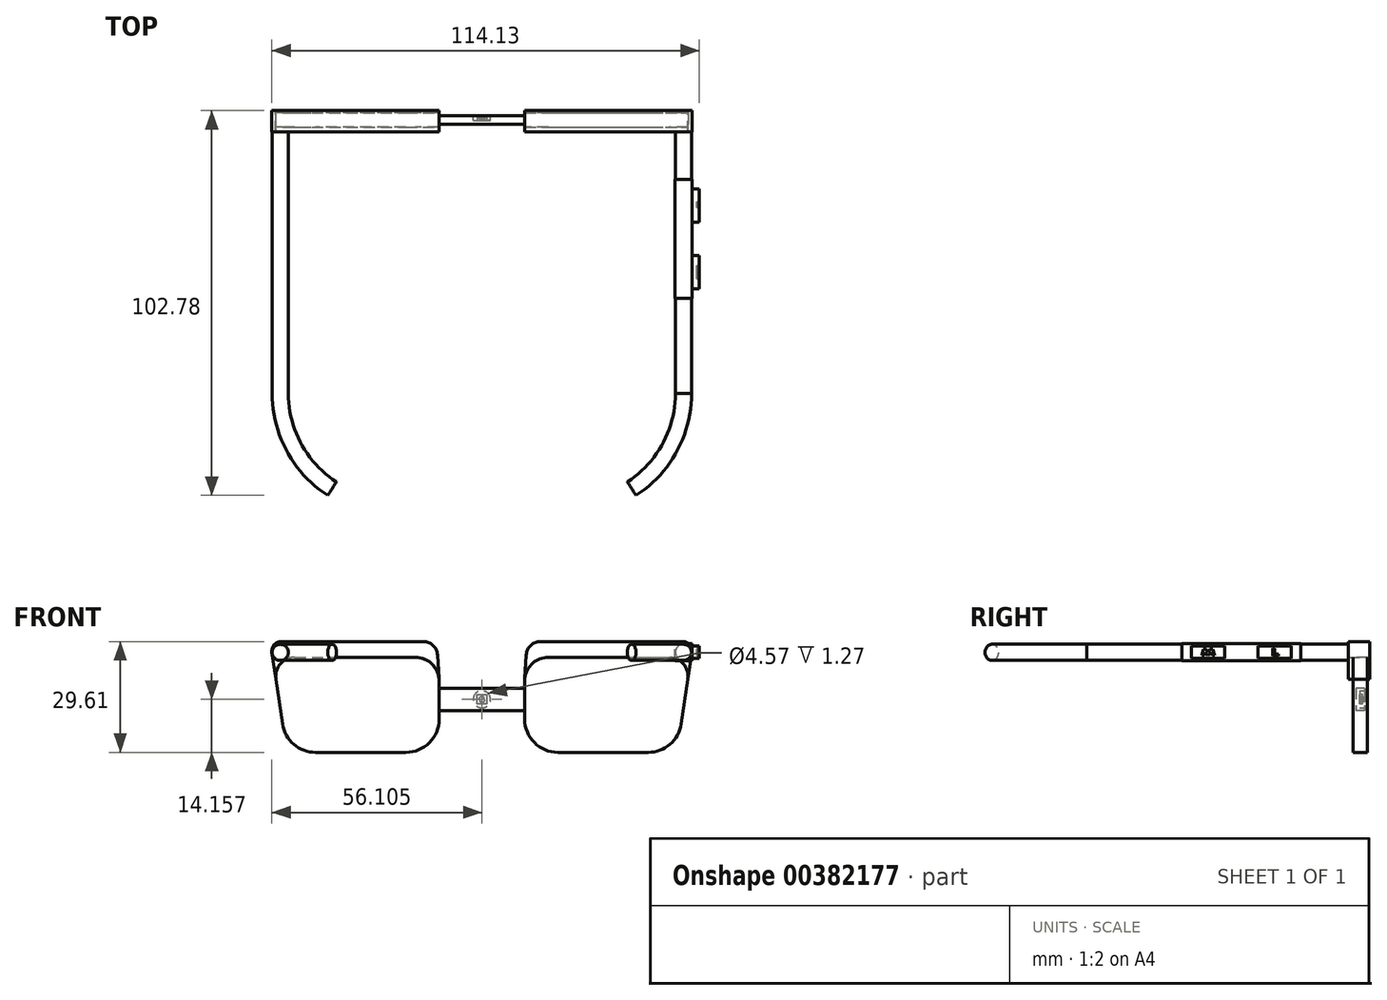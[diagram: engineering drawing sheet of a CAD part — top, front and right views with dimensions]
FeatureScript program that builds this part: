
annotation { "Feature Type Name" : "Feature", "Feature Type Description" : "" }
export const myFeature = defineFeature(function(context is Context, id is Id, definition is map)
    precondition{}
    {
        {
            var Q0;
            Q0=qCreatedBy(makeId("Front.planeOp"),FACE);
            var sketch = newSketch(context, id + "F0", { "sketchPlane" : qUnion([Q0])});
            skLineSegment(sketch, "E0", {"start": v(-55.04, 50.03) * mm, "end": v(-22.83, 50.03) * mm});
            skLineSegment(sketch, "E1", {"start": v(-16.48, 43.68) * mm, "end": v(-16.48, 33.52) * mm});
            skLineSegment(sketch, "E2", {"start": v(-25.37, 24.63) * mm, "end": v(-49.47, 24.63) * mm});
            skLineSegment(sketch, "E3", {"start": v(-58.26, 32.2) * mm, "end": v(-60.06, 44.2) * mm});
            skLineSegment(sketch, "E4", {"start": v(6.38, 43.68) * mm, "end": v(6.38, 33.52) * mm});
            skLineSegment(sketch, "E5", {"start": v(12.73, 50.03) * mm, "end": v(44.93, 50.03) * mm});
            skLineSegment(sketch, "E6", {"start": v(15.27, 24.63) * mm, "end": v(39.36, 24.63) * mm});
            skLineSegment(sketch, "E7", {"start": v(48.15, 32.2) * mm, "end": v(49.95, 44.2) * mm});
            skPoint(sketch, "E8.visualSharp", {"position": v(-16.48, 50.03) * mm});
            skArc(sketch, "E8.filletArc", {"start": v(-16.48, 43.68) * mm, "mid": v(-18.34, 48.17) * mm, "end": v(-22.83, 50.03) * mm});
            skPoint(sketch, "E9.visualSharp", {"position": v(6.38, 50.03) * mm});
            skArc(sketch, "E9.filletArc", {"start": v(12.73, 50.03) * mm, "mid": v(8.23, 48.17) * mm, "end": v(6.38, 43.68) * mm});
            skPoint(sketch, "E10.visualSharp", {"position": v(-16.48, 24.63) * mm});
            skArc(sketch, "E10.filletArc", {"start": v(-25.37, 24.63) * mm, "mid": v(-19.09, 27.23) * mm, "end": v(-16.48, 33.52) * mm});
            skPoint(sketch, "E11.visualSharp", {"position": v(-57.12, 24.63) * mm});
            skArc(sketch, "E11.filletArc", {"start": v(-58.26, 32.2) * mm, "mid": v(-55.27, 26.78) * mm, "end": v(-49.47, 24.63) * mm});
            skPoint(sketch, "E12.visualSharp", {"position": v(6.38, 24.63) * mm});
            skArc(sketch, "E12.filletArc", {"start": v(6.38, 33.52) * mm, "mid": v(8.98, 27.23) * mm, "end": v(15.27, 24.63) * mm});
            skPoint(sketch, "E13.visualSharp", {"position": v(47.02, 24.63) * mm});
            skArc(sketch, "E13.filletArc", {"start": v(39.36, 24.63) * mm, "mid": v(45.16, 26.78) * mm, "end": v(48.15, 32.2) * mm});
            skPoint(sketch, "E14.visualSharp", {"position": v(-60.93, 50.03) * mm});
            skArc(sketch, "E14.filletArc", {"start": v(-55.04, 50.03) * mm, "mid": v(-58.89, 48.26) * mm, "end": v(-60.06, 44.2) * mm});
            skPoint(sketch, "E15.visualSharp", {"position": v(50.83, 50.03) * mm});
            skArc(sketch, "E15.filletArc", {"start": v(49.95, 44.2) * mm, "mid": v(48.78, 48.26) * mm, "end": v(44.93, 50.03) * mm});
            skLineSegment(sketch, "E16", {"start": v(-16.48, 41.77) * mm, "end": v(6.38, 41.77) * mm});
            skLineSegment(sketch, "E17", {"start": v(-16.48, 35.8) * mm, "end": v(6.38, 35.8) * mm});
            skSolve(sketch);
        }
        {
            var Q0;
            Q0=makeQuery(id+"F0.imprint","IMPRINT",FACE,{"disambiguationData":[TD([[makeQuery(id+"F0.imprint","IMPRINT",EDGE,{"derivedFrom":sQuery(id+"F0.wireOp",EDGE,"E0")}),-1.0]])]});
            var Q1;
            Q1=makeQuery(id+"F0.imprint","IMPRINT",FACE,{"disambiguationData":[TD([[makeQuery(id+"F0.imprint","IMPRINT",EDGE,{"derivedFrom":sQuery(id+"F0.wireOp",EDGE,"E5")}),-1.0]])]});
            extrude(context, id + "F1", {"entities" : qUnion([Q0, Q1]), "oppositeDirection" : true, "depth" : 3.8 * mm});
        }
        {
            var Q0;
            {var subQ0=sQuery(id+"F0.wireOp",EDGE,"E16");Q0=makeQuery(id+"F0.imprint","IMPRINT",FACE,{"disambiguationData":[TD([[makeQuery(id+"F0.imprint","IMPRINT",EDGE,{"derivedFrom":subQ0}),-1.0]])]});}
            extrude(context, id + "F2", {"entities" : qUnion([Q0]), "oppositeDirection" : true, "depth" : 3.05 * mm});
        }
        {
            var Q0;
            Q0=makeQuery(id+"F2.opExtrude","CAP_FACE",FACE,{"disambiguationData":[OSD([sQuery(id+"F0.wireOp",EDGE,"E1"),sQuery(id+"F0.wireOp",EDGE,"E4"),sQuery(id+"F0.wireOp",EDGE,"E16"),sQuery(id+"F0.wireOp",EDGE,"E17")])],"isStart":true});
            extrude(context, id + "F3", {"entities" : qUnion([Q0]), "operationType" : NewBodyOperationType.REMOVE, "oppositeDirection" : true, "depth" : 0.76 * mm});
        }
        {
            var Q0;
            Q0=qCreatedBy(makeId("Front.planeOp"),FACE);
            var sketch = newSketch(context, id + "F4", { "sketchPlane" : qUnion([Q0])});
            skLineSegment(sketch, "E18.0", {"start": v(-55.04, 50.03) * mm, "end": v(-22.83, 50.03) * mm});
            skArc(sketch, "E19.0", {"start": v(-55.04, 50.03) * mm, "mid": v(-58.89, 48.26) * mm, "end": v(-60.06, 44.2) * mm});
            skArc(sketch, "E20.0", {"start": v(-16.48, 43.68) * mm, "mid": v(-18.34, 48.17) * mm, "end": v(-22.83, 50.03) * mm});
            skArc(sketch, "E21.0", {"start": v(12.73, 50.03) * mm, "mid": v(8.23, 48.17) * mm, "end": v(6.38, 43.68) * mm});
            skLineSegment(sketch, "E22.0", {"start": v(12.73, 50.03) * mm, "end": v(44.93, 50.03) * mm});
            skArc(sketch, "E23.0", {"start": v(49.95, 44.2) * mm, "mid": v(48.78, 48.26) * mm, "end": v(44.93, 50.03) * mm});
            skLineSegment(sketch, "E24", {"start": v(-60.06, 44.2) * mm, "end": v(-61.13, 51.32) * mm});
            skLineSegment(sketch, "E25", {"start": v(49.95, 44.2) * mm, "end": v(51.02, 51.32) * mm});
            skLineSegment(sketch, "E26", {"start": v(-58.62, 54.24) * mm, "end": v(-20.7, 54.24) * mm});
            skLineSegment(sketch, "E27", {"start": v(48.5, 54.24) * mm, "end": v(10.6, 54.24) * mm});
            skLineSegment(sketch, "E28", {"start": v(-16.9, 50.66) * mm, "end": v(-16.48, 43.68) * mm});
            skLineSegment(sketch, "E29", {"start": v(6.8, 50.66) * mm, "end": v(6.38, 43.68) * mm});
            skPoint(sketch, "E30.visualSharp", {"position": v(-61.57, 54.24) * mm});
            skArc(sketch, "E30.filletArc", {"start": v(-58.62, 54.24) * mm, "mid": v(-60.54, 53.36) * mm, "end": v(-61.13, 51.32) * mm});
            skPoint(sketch, "E31.visualSharp", {"position": v(-17.12, 54.24) * mm});
            skArc(sketch, "E31.filletArc", {"start": v(-16.9, 50.66) * mm, "mid": v(-18.1, 53.2) * mm, "end": v(-20.7, 54.24) * mm});
            skPoint(sketch, "E32.visualSharp", {"position": v(7, 54.24) * mm});
            skArc(sketch, "E32.filletArc", {"start": v(10.6, 54.24) * mm, "mid": v(7.98, 53.2) * mm, "end": v(6.8, 50.66) * mm});
            skPoint(sketch, "E33.visualSharp", {"position": v(51.46, 54.24) * mm});
            skArc(sketch, "E33.filletArc", {"start": v(51.02, 51.32) * mm, "mid": v(50.43, 53.36) * mm, "end": v(48.5, 54.24) * mm});
            skSolve(sketch);
        }
        {
            var Q0;
            {var subQ1=sQuery(id+"F4.wireOp",EDGE,"E18.0");Q0=makeQuery(id+"F4.imprint","IMPRINT",FACE,{"disambiguationData":[TD([[makeQuery(id+"F4.imprint","IMPRINT",EDGE,{"derivedFrom":subQ1}),1.0]])]});}
            var Q1;
            {var subQ1=sQuery(id+"F4.wireOp",EDGE,"E22.0");Q1=makeQuery(id+"F4.imprint","IMPRINT",FACE,{"disambiguationData":[TD([[makeQuery(id+"F4.imprint","IMPRINT",EDGE,{"derivedFrom":subQ1}),1.0]])]});}
            extrude(context, id + "F5", {"entities" : qUnion([Q0, Q1]), "depth" : 1.27 * mm, "hasSecondDirection" : true, "secondDirectionOppositeDirection" : true, "secondDirectionDepth" : 4.44 * mm});
        }
        {
            var Q0;
            Q0=makeQuery(id+"F5.opExtrude","CAP_FACE",FACE,{"disambiguationData":[OSD([sQuery(id+"F4.wireOp",EDGE,"E18.0"),sQuery(id+"F4.wireOp",EDGE,"E19.0"),sQuery(id+"F4.wireOp",EDGE,"E20.0"),sQuery(id+"F4.wireOp",EDGE,"E24"),sQuery(id+"F4.wireOp",EDGE,"E26"),sQuery(id+"F4.wireOp",EDGE,"E28"),sQuery(id+"F4.wireOp",EDGE,"E30.filletArc"),sQuery(id+"F4.wireOp",EDGE,"E31.filletArc")])],"isStart":false});
            var sketch = newSketch(context, id + "F6", { "sketchPlane" : qUnion([Q0])});
            skCircle(sketch, "E34", {"center": v(-58.89, 51.32) * mm, "radius": 2.16 * mm});
            skPoint(sketch, "E34.centerSnap0", {"position": v(-58.89, 48.26) * mm});
            skLineSegment(sketch, "E35.0", {"start": v(49.95, 44.2) * mm, "end": v(51.02, 51.32) * mm});
            skArc(sketch, "E36.0", {"start": v(49.95, 44.2) * mm, "mid": v(48.78, 48.26) * mm, "end": v(44.93, 50.03) * mm});
            skCircle(sketch, "E37", {"center": v(48.78, 51.32) * mm, "radius": 2.16 * mm});
            skPoint(sketch, "E37.centerSnap0", {"position": v(48.78, 48.26) * mm});
            skSolve(sketch);
        }
        {
            var Q0;
            Q0=makeQuery(id+"F6.imprint","IMPRINT",FACE,{"disambiguationData":[TD([[makeQuery(id+"F6.imprint","IMPRINT",EDGE,{"derivedFrom":sQuery(id+"F6.wireOp",EDGE,"E34")}),1.0]])]});
            extrude(context, id + "F7", {"entities" : qUnion([Q0]), "operationType" : NewBodyOperationType.ADD, "depth" : 69.85 * mm});
        }
        {
            var Q0;
            Q0=makeQuery(id+"F6.imprint","IMPRINT",FACE,{"disambiguationData":[TD([[makeQuery(id+"F6.imprint","IMPRINT",EDGE,{"derivedFrom":sQuery(id+"F6.wireOp",EDGE,"E37")}),1.0]])]});
            extrude(context, id + "F8", {"entities" : qUnion([Q0]), "depth" : 12.7 * mm});
        }
        {
            var Q0;
            Q0=makeQuery(id+"F8.opExtrude","CAP_FACE",FACE,{"disambiguationData":[OSD([sQuery(id+"F6.wireOp",EDGE,"E37")])],"isStart":false});
            var sketch = newSketch(context, id + "F9", { "sketchPlane" : qUnion([Q0])});
            skLineSegment(sketch, "E38", {"start": v(48.78, 51.32) * mm, "end": v(46.49, 51.32) * mm});
            skLineSegment(sketch, "E39", {"start": v(48.78, 51.32) * mm, "end": v(48.78, 49.04) * mm});
            skLineSegment(sketch, "E40", {"start": v(46.49, 51.32) * mm, "end": v(46.49, 49.04) * mm});
            skLineSegment(sketch, "E41", {"start": v(46.49, 49.04) * mm, "end": v(48.78, 49.04) * mm});
            skLineSegment(sketch, "E42", {"start": v(46.49, 51.32) * mm, "end": v(46.49, 53.6) * mm});
            skLineSegment(sketch, "E43", {"start": v(46.49, 53.6) * mm, "end": v(51.06, 53.6) * mm});
            skLineSegment(sketch, "E44", {"start": v(51.06, 53.6) * mm, "end": v(51.06, 49.04) * mm});
            skLineSegment(sketch, "E45", {"start": v(51.06, 49.04) * mm, "end": v(48.78, 49.04) * mm});
            skSolve(sketch);
        }
        {
            var Q0;
            {var subQ4=sQuery(id+"F9.wireOp",EDGE,"E42");Q0=makeQuery(id+"F9.imprint","IMPRINT",FACE,{"disambiguationData":[TD([[makeQuery(id+"F9.imprint","IMPRINT",EDGE,{"derivedFrom":subQ4}),-1.0]])]});}
            var Q1;
            {var subQ0=sQuery(id+"F9.wireOp",EDGE,"E39");var subQ1=sQuery(id+"F9.wireOp",EDGE,"E38");var subQ2=makeQuery(id+"F9.imprint","INTERSECT",VERTEX,{"derivedFrom":[subQ1,subQ0]});Q1=makeQuery(id+"F9.imprint","IMPRINT",FACE,{"disambiguationData":[TD([[makeQuery(id+"F9.imprint","IMPRINT",EDGE,{"disambiguationData":[TD([[subQ2,-1.0]])],"derivedFrom":subQ1}),-1.0]])]});}
            var Q2;
            {var subQ0=sQuery(id+"F9.wireOp",EDGE,"E39");var subQ1=sQuery(id+"F9.wireOp",EDGE,"E38");var subQ2=makeQuery(id+"F9.imprint","INTERSECT",VERTEX,{"derivedFrom":[subQ1,subQ0]});Q2=makeQuery(id+"F9.imprint","IMPRINT",FACE,{"disambiguationData":[TD([[makeQuery(id+"F9.imprint","IMPRINT",EDGE,{"disambiguationData":[TD([[subQ2,-1.0]])],"derivedFrom":subQ1}),1.0]])]});}
            var Q3;
            {var subQ1=sQuery(id+"F9.wireOp",EDGE,"E40");Q3=makeQuery(id+"F9.imprint","IMPRINT",FACE,{"disambiguationData":[TD([[makeQuery(id+"F9.imprint","IMPRINT",EDGE,{"derivedFrom":subQ1}),1.0]])]});}
            extrude(context, id + "F10", {"entities" : qUnion([Q0, Q1, Q2, Q3]), "operationType" : NewBodyOperationType.ADD, "depth" : 31.75 * mm});
        }
        {
            var Q0;
            Q0=makeQuery(id+"F10.opExtrude","CAP_FACE",FACE,{"disambiguationData":[OSD([sQuery(id+"F9.wireOp",EDGE,"E40"),sQuery(id+"F9.wireOp",EDGE,"E41"),sQuery(id+"F9.wireOp",EDGE,"E42"),sQuery(id+"F9.wireOp",EDGE,"E43"),sQuery(id+"F9.wireOp",EDGE,"E44"),sQuery(id+"F9.wireOp",EDGE,"E45")])],"isStart":false});
            var sketch = newSketch(context, id + "F11", { "sketchPlane" : qUnion([Q0])});
            skCircle(sketch, "E46", {"center": v(48.78, 51.32) * mm, "radius": 2.16 * mm});
            skPoint(sketch, "E46.centerSnap0", {"position": v(51.06, 51.32) * mm});
            skPoint(sketch, "E46.centerSnap1", {"position": v(48.78, 49.04) * mm});
            skSolve(sketch);
        }
        {
            var Q0;
            Q0=makeQuery(id+"F11.imprint","IMPRINT",FACE,{"disambiguationData":[TD([[makeQuery(id+"F11.imprint","IMPRINT",EDGE,{"derivedFrom":sQuery(id+"F11.wireOp",EDGE,"E46")}),1.0]])]});
            extrude(context, id + "F12", {"entities" : qUnion([Q0]), "operationType" : NewBodyOperationType.ADD, "depth" : 25.4 * mm});
        }
        {
            var Q0;
            Q0=makeQuery(id+"F2.opExtrude","CAP_FACE",FACE,{"disambiguationData":[OSD([sQuery(id+"F0.wireOp",EDGE,"E1"),sQuery(id+"F0.wireOp",EDGE,"E4"),sQuery(id+"F0.wireOp",EDGE,"E16"),sQuery(id+"F0.wireOp",EDGE,"E17")])],"isStart":false});
            var sketch = newSketch(context, id + "F13", { "sketchPlane" : qUnion([Q0])});
            skCircle(sketch, "E47", {"center": v(5.05, 38.79) * mm, "radius": 2.29 * mm});
            skPoint(sketch, "E47.centerSnap0", {"position": v(5.05, 35.8) * mm});
            skPoint(sketch, "E47.centerSnap1", {"position": v(-6.38, 38.79) * mm});
            skSolve(sketch);
        }
        {
            var Q0;
            Q0=makeQuery(id+"F13.imprint","IMPRINT",FACE,{"disambiguationData":[TD([[makeQuery(id+"F13.imprint","IMPRINT",EDGE,{"derivedFrom":sQuery(id+"F13.wireOp",EDGE,"E47")}),1.0]])]});
            extrude(context, id + "F14", {"entities" : qUnion([Q0]), "operationType" : NewBodyOperationType.REMOVE, "oppositeDirection" : true, "depth" : 1.27 * mm});
        }
        {
            var Q0;
            Q0=makeQuery(id+"F14.boolean.opBoolean","COPY",FACE,{"derivedFrom":makeQuery(id+"F14.opExtrude","CAP_FACE",FACE,{"disambiguationData":[OSD([sQuery(id+"F13.wireOp",EDGE,"E47")])],"isStart":false})});
            var sketch = newSketch(context, id + "F15", { "sketchPlane" : qUnion([Q0])});
            skLineSegment(sketch, "E48", {"start": v(5.05, 38.79) * mm, "end": v(6.32, 38.79) * mm});
            skLineSegment(sketch, "E49", {"start": v(6.32, 38.79) * mm, "end": v(6.32, 40.06) * mm});
            skLineSegment(sketch, "E50", {"start": v(6.32, 40.06) * mm, "end": v(3.8, 40.06) * mm});
            skLineSegment(sketch, "E51", {"start": v(3.8, 40.06) * mm, "end": v(3.8, 37.52) * mm});
            skLineSegment(sketch, "E52", {"start": v(3.8, 37.52) * mm, "end": v(6.32, 37.52) * mm});
            skLineSegment(sketch, "E53", {"start": v(6.32, 37.52) * mm, "end": v(6.32, 38.79) * mm});
            skSolve(sketch);
        }
        {
            var Q0;
            Q0=makeQuery(id+"F15.imprint","IMPRINT",FACE,{"disambiguationData":[TD([[makeQuery(id+"F15.imprint","IMPRINT",EDGE,{"derivedFrom":sQuery(id+"F15.wireOp",EDGE,"E49")}),1.0]])]});
            extrude(context, id + "F16", {"entities" : qUnion([Q0]), "operationType" : NewBodyOperationType.ADD, "depth" : 0.76 * mm});
        }
        {
            var Q0;
            Q0=makeQuery(id+"F16.opExtrude","CAP_FACE",FACE,{"disambiguationData":[OSD([sQuery(id+"F15.wireOp",EDGE,"E49"),sQuery(id+"F15.wireOp",EDGE,"E50"),sQuery(id+"F15.wireOp",EDGE,"E51"),sQuery(id+"F15.wireOp",EDGE,"E52"),sQuery(id+"F15.wireOp",EDGE,"E53")])],"isStart":false});
            var sketch = newSketch(context, id + "F17", { "sketchPlane" : qUnion([Q0])});
            skCircle(sketch, "E54.cCircle", {"center": v(5.06, 38.79) * mm, "radius": 0.7 * mm, "construction": true});
            skPoint(sketch, "E54.cCircle.centerSnap0", {"position": v(5.06, 37.52) * mm});
            skPoint(sketch, "E54.cCircle.centerSnap1", {"position": v(3.8, 38.79) * mm});
            skLineSegment(sketch, "E54.0", {"start": v(5.75, 38.37) * mm, "end": v(5.04, 37.98) * mm});
            skLineSegment(sketch, "E54.1", {"start": v(5.04, 37.98) * mm, "end": v(4.35, 38.4) * mm});
            skLineSegment(sketch, "E54.2", {"start": v(4.35, 38.4) * mm, "end": v(4.37, 39.2) * mm});
            skLineSegment(sketch, "E54.3", {"start": v(4.37, 39.2) * mm, "end": v(5.08, 39.6) * mm});
            skLineSegment(sketch, "E54.4", {"start": v(5.08, 39.6) * mm, "end": v(5.77, 39.17) * mm});
            skLineSegment(sketch, "E54.5", {"start": v(5.77, 39.17) * mm, "end": v(5.75, 38.37) * mm});
            skPoint(sketch, "E54.0.midPoint", {"position": v(5.4, 38.18) * mm});
            skSolve(sketch);
        }
        {
            var Q0;
            Q0=makeQuery(id+"F17.imprint","IMPRINT",FACE,{"disambiguationData":[TD([[makeQuery(id+"F17.imprint","IMPRINT",EDGE,{"derivedFrom":sQuery(id+"F17.wireOp",EDGE,"E54.0")}),-1.0]])]});
            extrude(context, id + "F18", {"entities" : qUnion([Q0]), "operationType" : NewBodyOperationType.REMOVE, "oppositeDirection" : true, "depth" : 0.38 * mm});
        }
        {
            var Q0;
            Q0=makeQuery(id+"F12.opExtrude","CAP_FACE",FACE,{"disambiguationData":[OSD([sQuery(id+"F11.wireOp",EDGE,"E46")])],"isStart":false});
            extrude(context, id + "F19", {"entities" : qUnion([Q0]), "depth" : 5.08 * mm});
        }
        {
            var Q0;
            Q0=makeQuery(id+"F19.opExtrude","SWEPT_BODY",BODY,{"disambiguationData":[OSD([sQuery(id+"F11.wireOp",EDGE,"E46")])]});
            deleteBodies(context, id + "F20", {"entities" : qUnion([Q0])});
        }
        {
            var Q0;
            Q0=makeQuery(id+"F10.opExtrude","SWEPT_FACE",FACE,{"disambiguationData":[OSD([sQuery(id+"F9.wireOp",EDGE,"E44")])]});
            var sketch = newSketch(context, id + "F21", { "sketchPlane" : qUnion([Q0])});
            skLineSegment(sketch, "E55.0", {"start": v(-45.72, 53.6) * mm, "end": v(-13.97, 53.6) * mm});
            skLineSegment(sketch, "E56.0", {"start": v(-45.72, 49.04) * mm, "end": v(-13.97, 49.04) * mm});
            skLineSegment(sketch, "E57.0", {"start": v(-13.97, 53.6) * mm, "end": v(-13.97, 49.04) * mm});
            skLineSegment(sketch, "E58.0", {"start": v(-45.72, 53.6) * mm, "end": v(-45.72, 49.04) * mm});
            skLineSegment(sketch, "E59", {"start": v(-29.85, 53.6) * mm, "end": v(-29.85, 49.04) * mm});
            skLineSegment(sketch, "E60", {"start": v(-37.78, 53.6) * mm, "end": v(-37.78, 49.04) * mm});
            skLineSegment(sketch, "E61", {"start": v(-21.9, 53.6) * mm, "end": v(-21.9, 49.04) * mm});
            skLineSegment(sketch, "E62", {"start": v(-45.72, 51.32) * mm, "end": v(-13.97, 51.32) * mm});
            skLineSegment(sketch, "E63", {"start": v(-43.18, 53.6) * mm, "end": v(-43.18, 49.04) * mm});
            skLineSegment(sketch, "E64", {"start": v(-34.3, 53.6) * mm, "end": v(-34.3, 49.04) * mm});
            skLineSegment(sketch, "E65", {"start": v(-25.4, 53.6) * mm, "end": v(-25.4, 49.04) * mm});
            skLineSegment(sketch, "E66", {"start": v(-16.51, 53.6) * mm, "end": v(-16.51, 49.04) * mm});
            skLineSegment(sketch, "E67", {"start": v(-25.4, 53.6) * mm, "end": v(-16.51, 53.6) * mm});
            skLineSegment(sketch, "E68", {"start": v(-25.4, 49.04) * mm, "end": v(-16.51, 49.04) * mm});
            skLineSegment(sketch, "E69", {"start": v(-43.18, 49.04) * mm, "end": v(-34.3, 49.04) * mm});
            skLineSegment(sketch, "E70", {"start": v(-43.18, 53.6) * mm, "end": v(-34.3, 53.6) * mm});
            skLineSegment(sketch, "E71", {"start": v(-43.18, 52.97) * mm, "end": v(-34.3, 52.97) * mm});
            skLineSegment(sketch, "E72", {"start": v(-43.18, 49.67) * mm, "end": v(-34.3, 49.67) * mm});
            skLineSegment(sketch, "E73", {"start": v(-25.4, 52.97) * mm, "end": v(-16.51, 52.97) * mm});
            skLineSegment(sketch, "E74", {"start": v(-25.4, 49.67) * mm, "end": v(-16.51, 49.67) * mm});
            skSolve(sketch);
        }
        {
            var Q0;
            {var subQ0=sQuery(id+"F21.wireOp",EDGE,"E71");var subQ1=sQuery(id+"F21.wireOp",EDGE,"E60");var subQ2=makeQuery(id+"F21.imprint","INTERSECT",VERTEX,{"derivedFrom":[subQ1,subQ0]});Q0=makeQuery(id+"F21.imprint","IMPRINT",FACE,{"disambiguationData":[TD([[makeQuery(id+"F21.imprint","IMPRINT",EDGE,{"disambiguationData":[TD([[subQ2,-1.0]])],"derivedFrom":subQ1}),-1.0]])]});}
            var Q1;
            {var subQ0=sQuery(id+"F21.wireOp",EDGE,"E62");var subQ1=sQuery(id+"F21.wireOp",EDGE,"E60");var subQ2=makeQuery(id+"F21.imprint","INTERSECT",VERTEX,{"derivedFrom":[subQ1,subQ0]});Q1=makeQuery(id+"F21.imprint","IMPRINT",FACE,{"disambiguationData":[TD([[makeQuery(id+"F21.imprint","IMPRINT",EDGE,{"disambiguationData":[TD([[subQ2,-1.0]])],"derivedFrom":subQ1}),-1.0]])]});}
            var Q2;
            {var subQ0=sQuery(id+"F21.wireOp",EDGE,"E71");var subQ1=sQuery(id+"F21.wireOp",EDGE,"E60");var subQ2=makeQuery(id+"F21.imprint","INTERSECT",VERTEX,{"derivedFrom":[subQ1,subQ0]});Q2=makeQuery(id+"F21.imprint","IMPRINT",FACE,{"disambiguationData":[TD([[makeQuery(id+"F21.imprint","IMPRINT",EDGE,{"disambiguationData":[TD([[subQ2,-1.0]])],"derivedFrom":subQ1}),1.0]])]});}
            var Q3;
            {var subQ0=sQuery(id+"F21.wireOp",EDGE,"E62");var subQ1=sQuery(id+"F21.wireOp",EDGE,"E60");var subQ2=makeQuery(id+"F21.imprint","INTERSECT",VERTEX,{"derivedFrom":[subQ1,subQ0]});Q3=makeQuery(id+"F21.imprint","IMPRINT",FACE,{"disambiguationData":[TD([[makeQuery(id+"F21.imprint","IMPRINT",EDGE,{"disambiguationData":[TD([[subQ2,-1.0]])],"derivedFrom":subQ1}),1.0]])]});}
            var Q4;
            {var subQ0=sQuery(id+"F21.wireOp",EDGE,"E73");var subQ1=sQuery(id+"F21.wireOp",EDGE,"E61");var subQ2=makeQuery(id+"F21.imprint","INTERSECT",VERTEX,{"derivedFrom":[subQ1,subQ0]});Q4=makeQuery(id+"F21.imprint","IMPRINT",FACE,{"disambiguationData":[TD([[makeQuery(id+"F21.imprint","IMPRINT",EDGE,{"disambiguationData":[TD([[subQ2,-1.0]])],"derivedFrom":subQ1}),-1.0]])]});}
            var Q5;
            {var subQ0=sQuery(id+"F21.wireOp",EDGE,"E62");var subQ1=sQuery(id+"F21.wireOp",EDGE,"E61");var subQ2=makeQuery(id+"F21.imprint","INTERSECT",VERTEX,{"derivedFrom":[subQ1,subQ0]});Q5=makeQuery(id+"F21.imprint","IMPRINT",FACE,{"disambiguationData":[TD([[makeQuery(id+"F21.imprint","IMPRINT",EDGE,{"disambiguationData":[TD([[subQ2,-1.0]])],"derivedFrom":subQ1}),-1.0]])]});}
            var Q6;
            {var subQ0=sQuery(id+"F21.wireOp",EDGE,"E73");var subQ1=sQuery(id+"F21.wireOp",EDGE,"E61");var subQ2=makeQuery(id+"F21.imprint","INTERSECT",VERTEX,{"derivedFrom":[subQ1,subQ0]});Q6=makeQuery(id+"F21.imprint","IMPRINT",FACE,{"disambiguationData":[TD([[makeQuery(id+"F21.imprint","IMPRINT",EDGE,{"disambiguationData":[TD([[subQ2,-1.0]])],"derivedFrom":subQ1}),1.0]])]});}
            var Q7;
            {var subQ0=sQuery(id+"F21.wireOp",EDGE,"E62");var subQ1=sQuery(id+"F21.wireOp",EDGE,"E61");var subQ2=makeQuery(id+"F21.imprint","INTERSECT",VERTEX,{"derivedFrom":[subQ1,subQ0]});Q7=makeQuery(id+"F21.imprint","IMPRINT",FACE,{"disambiguationData":[TD([[makeQuery(id+"F21.imprint","IMPRINT",EDGE,{"disambiguationData":[TD([[subQ2,-1.0]])],"derivedFrom":subQ1}),1.0]])]});}
            extrude(context, id + "F22", {"entities" : qUnion([Q0, Q1, Q2, Q3, Q4, Q5, Q6, Q7]), "depth" : 1.9 * mm});
        }
        {
            var Q0;
            Q0=makeQuery(id+"F22.opExtrude","CAP_FACE",FACE,{"disambiguationData":[OSD([sQuery(id+"F21.wireOp",EDGE,"E65"),sQuery(id+"F21.wireOp",EDGE,"E66"),sQuery(id+"F21.wireOp",EDGE,"E73"),sQuery(id+"F21.wireOp",EDGE,"E74")])],"isStart":false});
            var sketch = newSketch(context, id + "F23", { "sketchPlane" : qUnion([Q0])});
            skLineSegment(sketch, "E75.0", {"start": v(-25.4, 52.97) * mm, "end": v(-16.51, 52.97) * mm});
            skLineSegment(sketch, "E76.0", {"start": v(-16.51, 52.97) * mm, "end": v(-16.51, 49.67) * mm});
            skLineSegment(sketch, "E77.0", {"start": v(-25.4, 49.67) * mm, "end": v(-16.51, 49.67) * mm});
            skLineSegment(sketch, "E78.0", {"start": v(-25.4, 52.97) * mm, "end": v(-25.4, 49.67) * mm});
            skLineSegment(sketch, "E79", {"start": v(-20.96, 52.97) * mm, "end": v(-20.96, 49.67) * mm});
            skLineSegment(sketch, "E80", {"start": v(-20.96, 50.81) * mm, "end": v(-19.94, 50.81) * mm});
            skLineSegment(sketch, "E81", {"start": v(-19.94, 50.81) * mm, "end": v(-19.94, 50.3) * mm});
            skLineSegment(sketch, "E82", {"start": v(-19.94, 50.3) * mm, "end": v(-20.96, 50.3) * mm});
            skLineSegment(sketch, "E83", {"start": v(-20.96, 52.34) * mm, "end": v(-21.46, 52.34) * mm});
            skLineSegment(sketch, "E84", {"start": v(-21.46, 52.34) * mm, "end": v(-21.46, 50.3) * mm});
            skLineSegment(sketch, "E85", {"start": v(-21.46, 50.3) * mm, "end": v(-20.96, 50.3) * mm});
            skSolve(sketch);
        }
        {
            var Q0;
            {var subQ0=sQuery(id+"F23.wireOp",EDGE,"E83");Q0=makeQuery(id+"F23.imprint","IMPRINT",FACE,{"disambiguationData":[TD([[makeQuery(id+"F23.imprint","IMPRINT",EDGE,{"derivedFrom":subQ0}),1.0]])]});}
            var Q1;
            {var subQ0=sQuery(id+"F23.wireOp",EDGE,"E80");Q1=makeQuery(id+"F23.imprint","IMPRINT",FACE,{"disambiguationData":[TD([[makeQuery(id+"F23.imprint","IMPRINT",EDGE,{"derivedFrom":subQ0}),-1.0]])]});}
            extrude(context, id + "F24", {"entities" : qUnion([Q0, Q1]), "operationType" : NewBodyOperationType.REMOVE, "oppositeDirection" : true, "depth" : 0.64 * mm});
        }
        {
            var Q0;
            Q0=makeQuery(id+"F22.opExtrude","CAP_FACE",FACE,{"disambiguationData":[OSD([sQuery(id+"F21.wireOp",EDGE,"E63"),sQuery(id+"F21.wireOp",EDGE,"E64"),sQuery(id+"F21.wireOp",EDGE,"E71"),sQuery(id+"F21.wireOp",EDGE,"E72")])],"isStart":false});
            var sketch = newSketch(context, id + "F25", { "sketchPlane" : qUnion([Q0])});
            skLineSegment(sketch, "E86.0", {"start": v(-43.18, 52.97) * mm, "end": v(-34.3, 52.97) * mm});
            skLineSegment(sketch, "E87.0", {"start": v(-34.3, 52.97) * mm, "end": v(-34.3, 49.67) * mm});
            skLineSegment(sketch, "E88.0", {"start": v(-43.18, 52.97) * mm, "end": v(-43.18, 49.67) * mm});
            skLineSegment(sketch, "E89.0", {"start": v(-43.18, 49.67) * mm, "end": v(-34.3, 49.67) * mm});
            skLineSegment(sketch, "E90", {"start": v(-38.74, 52.97) * mm, "end": v(-38.74, 49.67) * mm});
            skLineSegment(sketch, "E91", {"start": v(-38.74, 51.32) * mm, "end": v(-39.24, 52.19) * mm});
            skLineSegment(sketch, "E92", {"start": v(-39.24, 52.19) * mm, "end": v(-38.23, 52.19) * mm});
            skLineSegment(sketch, "E93", {"start": v(-38.74, 51.32) * mm, "end": v(-38.23, 52.19) * mm});
            skLineSegment(sketch, "E94", {"start": v(-38.23, 52.19) * mm, "end": v(-37.47, 52.19) * mm});
            skLineSegment(sketch, "E95", {"start": v(-39.24, 52.19) * mm, "end": v(-40, 52.19) * mm});
            skLineSegment(sketch, "E96", {"start": v(-40, 52.19) * mm, "end": v(-40.48, 50.47) * mm});
            skLineSegment(sketch, "E97", {"start": v(-40.48, 50.47) * mm, "end": v(-36.99, 50.47) * mm});
            skLineSegment(sketch, "E98", {"start": v(-36.99, 50.47) * mm, "end": v(-37.47, 52.19) * mm});
            skLineSegment(sketch, "E99", {"start": v(-39.87, 50.47) * mm, "end": v(-39.57, 51.32) * mm});
            skLineSegment(sketch, "E100", {"start": v(-39.57, 51.32) * mm, "end": v(-38.74, 50.47) * mm});
            skLineSegment(sketch, "E101", {"start": v(-38.74, 50.47) * mm, "end": v(-37.87, 51.32) * mm});
            skLineSegment(sketch, "E102", {"start": v(-37.87, 51.32) * mm, "end": v(-37.6, 50.47) * mm});
            skSolve(sketch);
        }
        {
            var Q0;
            {var subQ1=sQuery(id+"F25.wireOp",EDGE,"E91");Q0=makeQuery(id+"F25.imprint","IMPRINT",FACE,{"disambiguationData":[TD([[makeQuery(id+"F25.imprint","IMPRINT",EDGE,{"derivedFrom":subQ1}),1.0]])]});}
            var Q1;
            {var subQ3=sQuery(id+"F25.wireOp",EDGE,"E93");Q1=makeQuery(id+"F25.imprint","IMPRINT",FACE,{"disambiguationData":[TD([[makeQuery(id+"F25.imprint","IMPRINT",EDGE,{"derivedFrom":subQ3}),-1.0]])]});}
            extrude(context, id + "F26", {"entities" : qUnion([Q0, Q1]), "operationType" : NewBodyOperationType.REMOVE, "oppositeDirection" : true, "depth" : 0.64 * mm});
        }
        {
            var Q0;
            Q0=makeQuery(id+"F12.opExtrude","CAP_FACE",FACE,{"disambiguationData":[OSD([sQuery(id+"F11.wireOp",EDGE,"E46")])],"isStart":false});
            var sketch = newSketch(context, id + "F27", { "sketchPlane" : qUnion([Q0])});
            skCircle(sketch, "E103.0", {"center": v(48.78, 51.32) * mm, "radius": 2.16 * mm});
            skSolve(sketch);
        }
        {
            var Q0;
            Q0=qCreatedBy(makeId("Top.planeOp"),FACE);
            var sketch = newSketch(context, id + "F28", { "sketchPlane" : qUnion([Q0])});
            skLineSegment(sketch, "E104.0", {"start": v(50.93, -71.12) * mm, "end": v(46.62, -71.12) * mm});
            skLineSegment(sketch, "E105", {"start": v(48.78, -71.12) * mm, "end": v(48.78, -96.52) * mm});
            skArc(sketch, "E106", {"start": v(34.93, -96.52) * mm, "mid": v(45.1, -85.58) * mm, "end": v(48.78, -71.12) * mm});
            skSolve(sketch);
        }
        {
            var Q0;
            Q0=makeQuery(id+"F27.imprint","IMPRINT",FACE,{"disambiguationData":[TD([[makeQuery(id+"F27.imprint","IMPRINT",EDGE,{"derivedFrom":sQuery(id+"F27.wireOp",EDGE,"E103.0")}),1.0]])]});
            var Q1;
            Q1=sQuery(id+"F28.wireOp",EDGE,"E106");
            sweep(context, id + "F29", {"profiles" : qUnion([Q0]), "path" : qUnion([Q1])});
        }
        {
            var Q0;
            Q0=makeQuery(id+"F7.opExtrude","CAP_FACE",FACE,{"disambiguationData":[OSD([sQuery(id+"F6.wireOp",EDGE,"E34")])],"isStart":false});
            var sketch = newSketch(context, id + "F30", { "sketchPlane" : qUnion([Q0])});
            skCircle(sketch, "E107.0", {"center": v(-58.89, 51.32) * mm, "radius": 2.16 * mm});
            skSolve(sketch);
        }
        {
            var Q0;
            Q0=qCreatedBy(makeId("Top.planeOp"),FACE);
            var sketch = newSketch(context, id + "F31", { "sketchPlane" : qUnion([Q0])});
            skLineSegment(sketch, "E108.0", {"start": v(-56.73, -71.12) * mm, "end": v(-61.04, -71.12) * mm});
            skLineSegment(sketch, "E109", {"start": v(-58.89, -71.12) * mm, "end": v(-58.89, -96.52) * mm});
            skArc(sketch, "E110", {"start": v(-58.89, -71.12) * mm, "mid": v(-55.2, -85.58) * mm, "end": v(-45.04, -96.52) * mm});
            skSolve(sketch);
        }
        {
            var Q0;
            Q0=makeQuery(id+"F30.imprint","IMPRINT",FACE,{"disambiguationData":[TD([[makeQuery(id+"F30.imprint","IMPRINT",EDGE,{"derivedFrom":sQuery(id+"F30.wireOp",EDGE,"E107.0")}),1.0]])]});
            var Q1;
            Q1=sQuery(id+"F31.wireOp",EDGE,"E110");
            sweep(context, id + "F32", {"operationType" : NewBodyOperationType.ADD, "profiles" : qUnion([Q0]), "path" : qUnion([Q1])});
        }
    });
